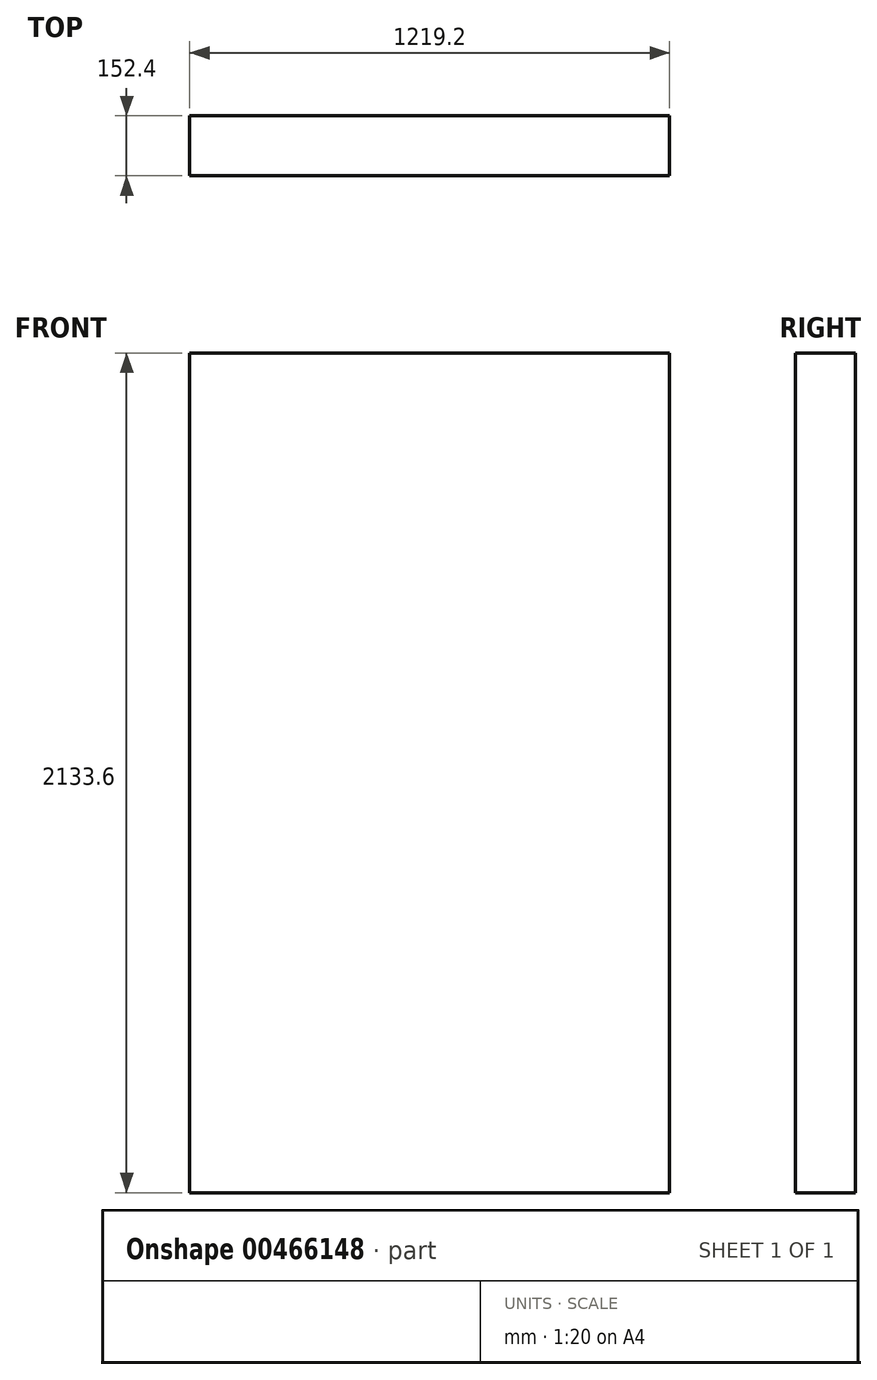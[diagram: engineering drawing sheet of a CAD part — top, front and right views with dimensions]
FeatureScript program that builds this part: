
annotation { "Feature Type Name" : "Feature", "Feature Type Description" : "" }
export const myFeature = defineFeature(function(context is Context, id is Id, definition is map)
    precondition{}
    {
        {
            assignVariable(context, id + "F0", {"name" : "DEPTH", "anyValue" : 152.4 * mm});
        }
        {
            var Q0;
            Q0=qCreatedBy(makeId("Front.planeOp"),FACE);
            var sketch = newSketch(context, id + "F1", { "sketchPlane" : qUnion([Q0])});
            skLineSegment(sketch, "E0.bottom", {"start": v(0, 0) * mm, "end": v(1219.2, 0) * mm});
            skLineSegment(sketch, "E0.top", {"start": v(0, 2133.6) * mm, "end": v(1219.2, 2133.6) * mm});
            skLineSegment(sketch, "E0.left", {"start": v(0, 0) * mm, "end": v(0, 2133.6) * mm});
            skLineSegment(sketch, "E0.right", {"start": v(1219.2, 0) * mm, "end": v(1219.2, 2133.6) * mm});
            skSolve(sketch);
        }
        {
            var Q0;
            Q0=makeQuery(id+"F1.imprint","IMPRINT",FACE,{"disambiguationData":[TD([[makeQuery(id+"F1.imprint","IMPRINT",EDGE,{"derivedFrom":sQuery(id+"F1.wireOp",EDGE,"E0.bottom")}),1.0]])]});
            extrude(context, id + "F2", {"entities" : qUnion([Q0]), "depth" : getVariable(context, 'DEPTH')});
        }
    });
